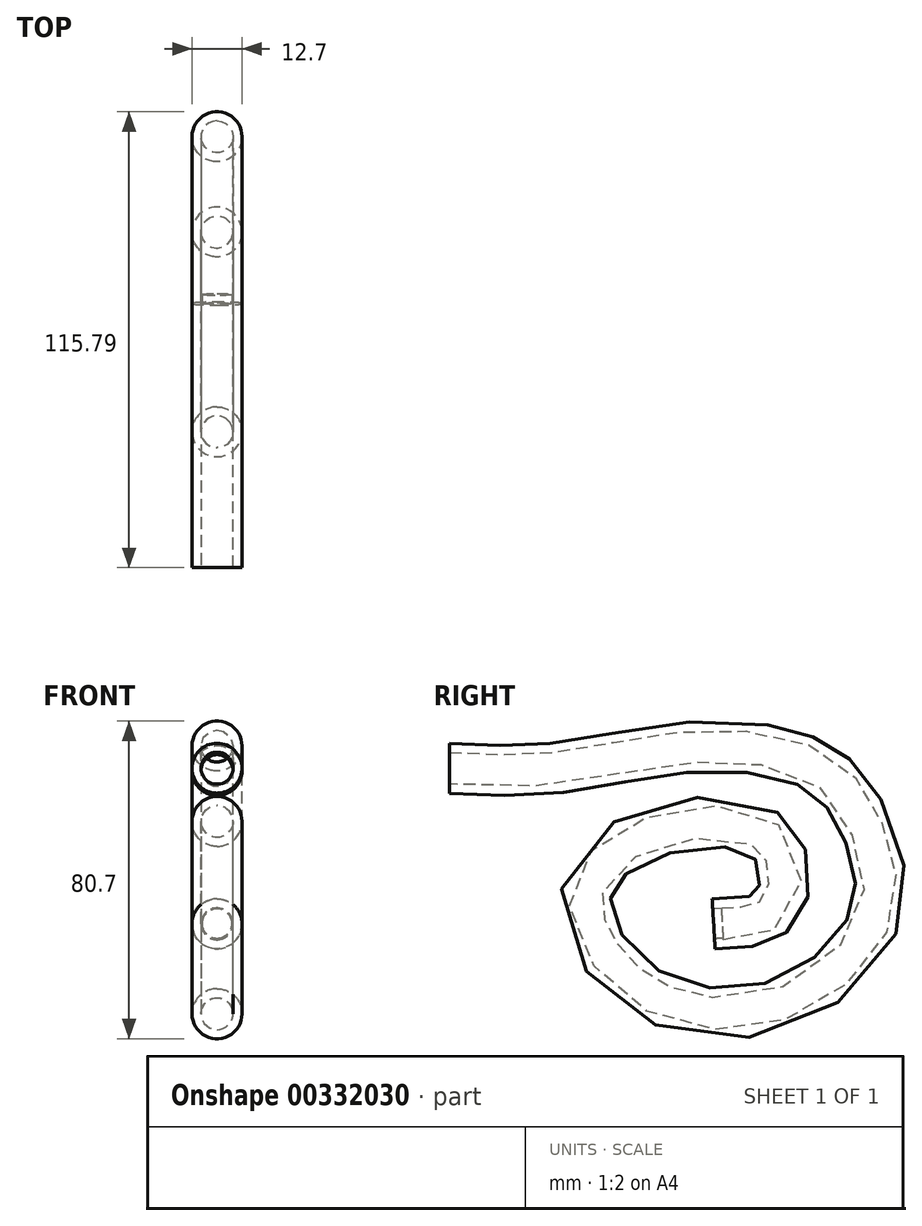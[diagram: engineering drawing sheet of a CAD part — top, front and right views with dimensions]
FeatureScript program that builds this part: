
annotation { "Feature Type Name" : "Feature", "Feature Type Description" : "" }
export const myFeature = defineFeature(function(context is Context, id is Id, definition is map)
    precondition{}
    {
        {
            var Q0;
            Q0=qCreatedBy(makeId("Front.planeOp"),FACE);
            var sketch = newSketch(context, id + "F0", { "sketchPlane" : qUnion([Q0])});
            skCircle(sketch, "E0", {"center": v(0, 0) * mm, "radius": 6.35 * mm});
            skSolve(sketch);
        }
        {
            var Q0;
            Q0=qCreatedBy(makeId("Right.planeOp"),FACE);
            var sketch = newSketch(context, id + "F1", { "sketchPlane" : qUnion([Q0])});
            skFitSpline(sketch, "E1", {"points": [v(0, 0) * mm, v(26.83, 0) * mm, v(61.9, 5.41) * mm, v(94.13, 0) * mm, v(106.37, -16.24) * mm, v(108.25, -37.65) * mm, v(84.72, -59.77) * mm, v(49.18, -56.48) * mm, v(34.6, -32.24) * mm, v(52.24, -16) * mm, v(81.9, -18.36) * mm, v(82.83, -35.53) * mm, v(67.07, -39.53) * mm], "startDerivative": vector(309.84, -18.9) * mm, "endDerivative": vector(-286.96, 0.36) * mm});
            skSolve(sketch);
        }
        {
            var Q0;
            Q0=makeQuery(id+"F0.imprint","IMPRINT",FACE,{"disambiguationData":[TD([[makeQuery(id+"F0.imprint","IMPRINT",EDGE,{"derivedFrom":sQuery(id+"F0.wireOp",EDGE,"E0")}),1.0]])]});
            var Q1;
            Q1=sQuery(id+"F1.wireOp",EDGE,"E1");
            sweep(context, id + "F2", {"profiles" : qUnion([Q0]), "path" : qUnion([Q1])});
        }
        {
            var Q0;
            Q0=makeQuery(id+"F2.opSweep","CAP_FACE",FACE,{"disambiguationData":[OSD([sQuery(id+"F0.wireOp",EDGE,"E0"),sQuery(id+"F1.wireOp",VERTEX,"E1.start")])],"isStart":true});
            shell(context, id + "F3", {"entities" : qUnion([Q0]), "thickness" : 2.3 * mm});
        }
        {
            var Q0;
            Q0=makeQuery(id+"F2.opSweep","CAP_FACE",FACE,{"disambiguationData":[OSD([sQuery(id+"F0.wireOp",EDGE,"E0"),sQuery(id+"F1.wireOp",VERTEX,"E1.end")])],"isStart":false});
            var sketch = newSketch(context, id + "F4", { "sketchPlane" : qUnion([Q0])});
            skCircle(sketch, "E2", {"center": v(0, -43.46) * mm, "radius": 4.9 * mm});
            skSolve(sketch);
        }
        {
            var Q0;
            Q0=makeQuery(id+"F4.imprint","IMPRINT",FACE,{"disambiguationData":[TD([[makeQuery(id+"F4.imprint","IMPRINT",EDGE,{"derivedFrom":sQuery(id+"F4.wireOp",EDGE,"E2")}),1.0]])]});
            extrude(context, id + "F5", {"entities" : qUnion([Q0]), "operationType" : NewBodyOperationType.REMOVE, "depth" : 2.03 * mm});
        }
        {
            var Q0;
            Q0=makeQuery(id+"F2.opSweep","CAP_FACE",FACE,{"disambiguationData":[OSD([sQuery(id+"F0.wireOp",EDGE,"E0"),sQuery(id+"F1.wireOp",VERTEX,"E1.end")])],"isStart":false});
            var sketch = newSketch(context, id + "F6", { "sketchPlane" : qUnion([Q0])});
            skCircle(sketch, "E3", {"center": v(0, -43.46) * mm, "radius": 3.81 * mm});
            skSolve(sketch);
        }
        {
            var Q0;
            Q0=makeQuery(id+"F6.imprint","IMPRINT",FACE,{"disambiguationData":[TD([[makeQuery(id+"F6.imprint","IMPRINT",EDGE,{"derivedFrom":sQuery(id+"F6.wireOp",EDGE,"E3")}),1.0]])]});
            var Q1;
            Q1=sQuery(id+"F6.wireOp",EDGE,"E3");
            extrude(context, id + "F7", {"entities" : qUnion([Q0]), "operationType" : NewBodyOperationType.REMOVE, "surfaceEntities" : qUnion([Q1]), "oppositeDirection" : true, "depth" : 2.3 * mm});
        }
    });
